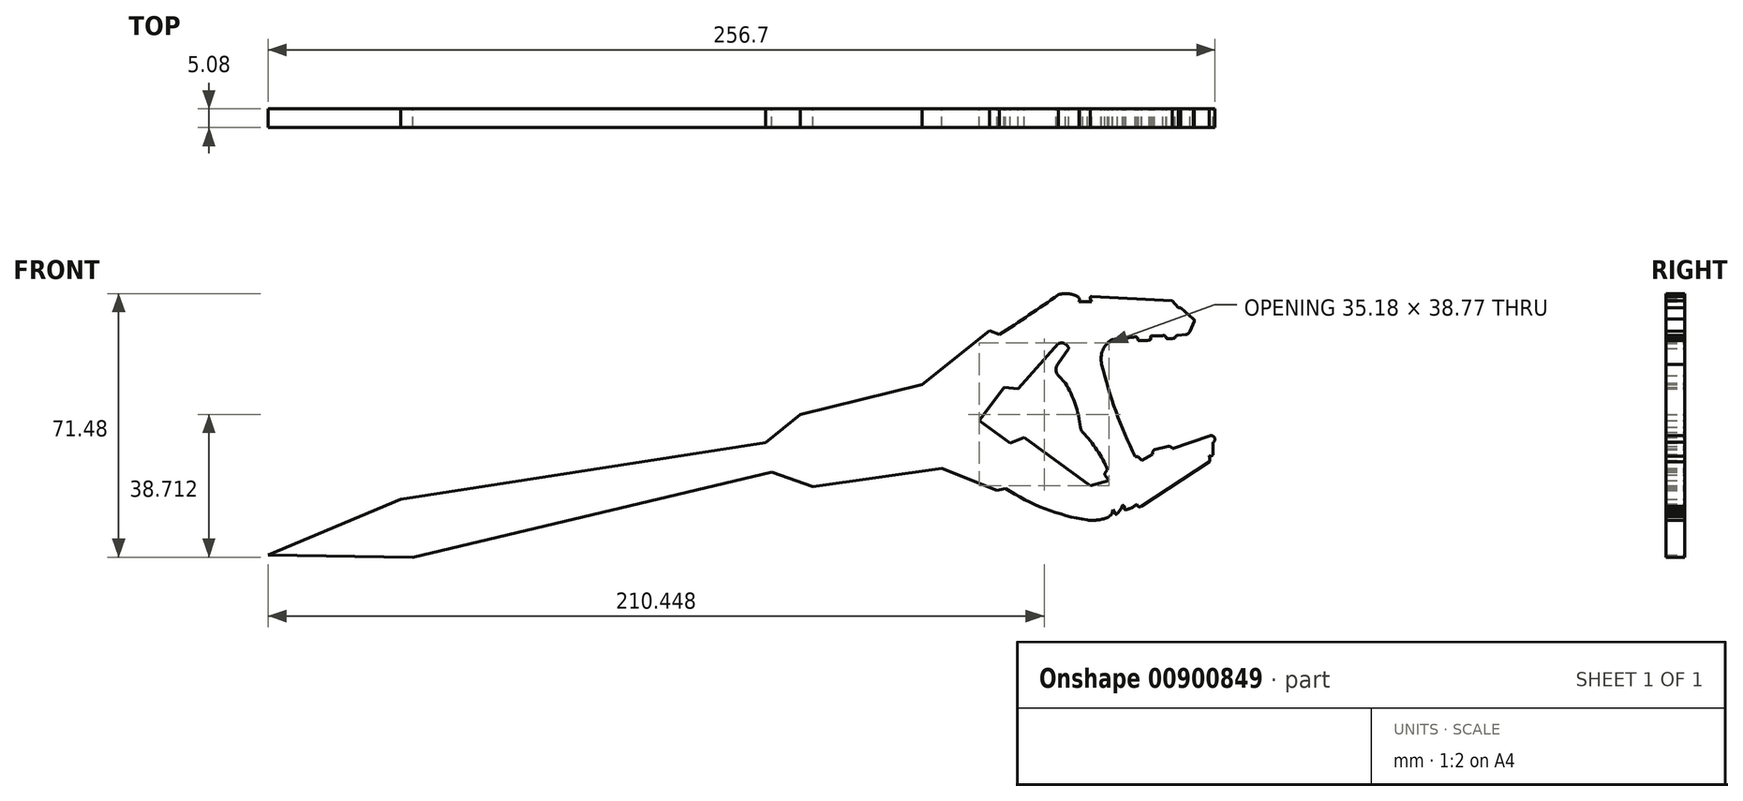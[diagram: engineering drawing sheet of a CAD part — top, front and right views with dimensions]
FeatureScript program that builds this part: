
annotation { "Feature Type Name" : "Feature", "Feature Type Description" : "" }
export const myFeature = defineFeature(function(context is Context, id is Id, definition is map)
    precondition{}
    {
        {
            var Q0;
            Q0=qCreatedBy(makeId("Front.planeOp"),FACE);
            var sketch = newSketch(context, id + "F0", { "sketchPlane" : qUnion([Q0])});
            skLineSegment(sketch, "E0", {"start": v(100.4, 44.75) * mm, "end": v(122.37, 43.65) * mm});
            skLineSegment(sketch, "E1", {"start": v(113.9, -12.05) * mm, "end": v(132.4, 0) * mm});
            skLineSegment(sketch, "E2", {"start": v(21.52, 12.73) * mm, "end": v(54.53, 20.95) * mm});
            skLineSegment(sketch, "E3", {"start": v(54.53, 20.95) * mm, "end": v(72.8, 35.55) * mm});
            skLineSegment(sketch, "E4", {"start": v(21.52, 12.73) * mm, "end": v(12.13, 5.19) * mm});
            skLineSegment(sketch, "E5", {"start": v(13.74, -2.79) * mm, "end": v(24.96, -6.78) * mm});
            skLineSegment(sketch, "E6", {"start": v(24.96, -6.78) * mm, "end": v(59.8, -1.87) * mm});
            skLineSegment(sketch, "E7", {"start": v(59.8, -1.87) * mm, "end": v(74.78, -7.84) * mm});
            skLineSegment(sketch, "E8", {"start": v(74.78, -7.84) * mm, "end": v(77.16, -7.24) * mm});
            skLineSegment(sketch, "E9", {"start": v(12.13, 5.19) * mm, "end": v(-86.83, -10.15) * mm});
            skLineSegment(sketch, "E10", {"start": v(-86.83, -10.15) * mm, "end": v(-122.84, -25.28) * mm});
            skLineSegment(sketch, "E11", {"start": v(72.8, 35.55) * mm, "end": v(75.47, 34.46) * mm});
            skLineSegment(sketch, "E12", {"start": v(76.66, 20.14) * mm, "end": v(70.02, 11.15) * mm});
            skLineSegment(sketch, "E13", {"start": v(70.02, 11.15) * mm, "end": v(78.32, 5.02) * mm});
            skLineSegment(sketch, "E14", {"start": v(78.32, 5.02) * mm, "end": v(82.2, 6.57) * mm});
            skLineSegment(sketch, "E15", {"start": v(82.2, 6.57) * mm, "end": v(100.16, -6.56) * mm});
            skLineSegment(sketch, "E16", {"start": v(100.16, -6.56) * mm, "end": v(105.2, -5.08) * mm});
            skLineSegment(sketch, "E17", {"start": v(76.66, 20.14) * mm, "end": v(81.19, 19.7) * mm});
            skLineSegment(sketch, "E18", {"start": v(91.5, 32.04) * mm, "end": v(80.58, 19.75) * mm});
            skLineSegment(sketch, "E19", {"start": v(105.2, -5.08) * mm, "end": v(104.05, -3.66) * mm});
            skArc(sketch, "E20", {"start": v(75.47, 34.46) * mm, "mid": v(83.52, 39.77) * mm, "end": v(91.45, 45.24) * mm});
            skArc(sketch, "E21", {"start": v(97.07, 44.48) * mm, "mid": v(94.35, 45.54) * mm, "end": v(91.45, 45.24) * mm});
            skArc(sketch, "E22", {"start": v(97.07, 43.35) * mm, "mid": v(97.13, 43.91) * mm, "end": v(97.07, 44.48) * mm});
            skLineSegment(sketch, "E23", {"start": v(97.07, 43.35) * mm, "end": v(100.5, 43.35) * mm});
            skLineSegment(sketch, "E24", {"start": v(100.5, 43.35) * mm, "end": v(100.14, 44.2) * mm});
            skArc(sketch, "E25", {"start": v(100.4, 44.75) * mm, "mid": v(100.1, 44.56) * mm, "end": v(100.14, 44.2) * mm});
            skArc(sketch, "E26", {"start": v(106.03, 33.12) * mm, "mid": v(103.5, 30.22) * mm, "end": v(103.2, 26.38) * mm});
            skArc(sketch, "E27", {"start": v(103.2, 26.38) * mm, "mid": v(107.04, 13.64) * mm, "end": v(112.26, 1.4) * mm});
            skArc(sketch, "E28", {"start": v(94.26, 30.67) * mm, "mid": v(93.2, 32) * mm, "end": v(91.5, 32.04) * mm});
            skArc(sketch, "E29", {"start": v(117.44, 3.2) * mm, "mid": v(117.03, 2.65) * mm, "end": v(117.05, 1.97) * mm});
            skLineSegment(sketch, "E30", {"start": v(117.44, 3.2) * mm, "end": v(121.18, 4.1) * mm});
            skArc(sketch, "E31", {"start": v(122.37, 3.54) * mm, "mid": v(121.87, 4.03) * mm, "end": v(121.18, 4.1) * mm});
            skLineSegment(sketch, "E32", {"start": v(122.37, 3.54) * mm, "end": v(132.3, 6.92) * mm});
            skArc(sketch, "E33", {"start": v(133.4, 5.23) * mm, "mid": v(133.7, 6.63) * mm, "end": v(132.3, 6.92) * mm});
            skLineSegment(sketch, "E34", {"start": v(133.4, 5.23) * mm, "end": v(133.4, 2.2) * mm});
            skArc(sketch, "E35", {"start": v(132.34, 1.6) * mm, "mid": v(133.05, 1.58) * mm, "end": v(133.4, 2.2) * mm});
            skArc(sketch, "E36", {"start": v(132.4, 0) * mm, "mid": v(132.48, 0.8) * mm, "end": v(132.34, 1.6) * mm});
            skArc(sketch, "E37", {"start": v(77.16, -7.24) * mm, "mid": v(87.78, -12.75) * mm, "end": v(99.34, -15.84) * mm});
            skArc(sketch, "E38", {"start": v(99.34, -15.84) * mm, "mid": v(102.3, -15.8) * mm, "end": v(105.12, -14.96) * mm});
            skPoint(sketch, "E39.start.orphan", {"position": v(107.25, -13.94) * mm});
            skPoint(sketch, "E40.orphan", {"position": v(107.24, -13.94) * mm});
            skPoint(sketch, "E41.end.orphan", {"position": v(105.95, -12.54) * mm});
            skPoint(sketch, "E42.end.orphan", {"position": v(105.95, -14.27) * mm});
            skArc(sketch, "E43", {"start": v(105.12, -14.96) * mm, "mid": v(105.9, -14.1) * mm, "end": v(106.18, -12.98) * mm});
            skLineSegment(sketch, "E44", {"start": v(106.18, -12.98) * mm, "end": v(106.77, -14.03) * mm});
            skArc(sketch, "E45", {"start": v(106.77, -14.03) * mm, "mid": v(107.1, -14.23) * mm, "end": v(107.44, -14.03) * mm});
            skArc(sketch, "E46", {"start": v(107.44, -14.03) * mm, "mid": v(108.28, -13.02) * mm, "end": v(108.82, -11.83) * mm});
            skArc(sketch, "E47", {"start": v(109.31, -12.56) * mm, "mid": v(109.27, -12.06) * mm, "end": v(108.82, -11.83) * mm});
            skArc(sketch, "E48", {"start": v(109.31, -12.56) * mm, "mid": v(109.4, -12.95) * mm, "end": v(109.78, -13.05) * mm});
            skArc(sketch, "E49", {"start": v(109.78, -13.05) * mm, "mid": v(111.4, -12.43) * mm, "end": v(112.85, -11.5) * mm});
            skArc(sketch, "E50", {"start": v(112.85, -11.5) * mm, "mid": v(113.16, -12.19) * mm, "end": v(113.9, -12.05) * mm});
            skLineSegment(sketch, "E51", {"start": v(117.05, 1.97) * mm, "end": v(114.12, 0.32) * mm});
            skLineSegment(sketch, "E52", {"start": v(114.12, 0.32) * mm, "end": v(113.04, 1.4) * mm});
            skLineSegment(sketch, "E53", {"start": v(113.04, 1.4) * mm, "end": v(112.26, 1.4) * mm});
            skArc(sketch, "E54", {"start": v(106.03, 33.12) * mm, "mid": v(109.29, 33.45) * mm, "end": v(112.53, 33.93) * mm});
            skArc(sketch, "E55", {"start": v(113, 33.07) * mm, "mid": v(112.86, 33.55) * mm, "end": v(112.53, 33.93) * mm});
            skArc(sketch, "E56", {"start": v(113, 33.07) * mm, "mid": v(113.02, 32.95) * mm, "end": v(113.11, 32.86) * mm});
            skArc(sketch, "E57", {"start": v(113.11, 32.86) * mm, "mid": v(114.6, 32.8) * mm, "end": v(116.1, 32.96) * mm});
            skArc(sketch, "E58", {"start": v(116.1, 32.96) * mm, "mid": v(116.3, 33.01) * mm, "end": v(116.44, 33.19) * mm});
            skArc(sketch, "E59", {"start": v(116.55, 34.17) * mm, "mid": v(116.48, 33.68) * mm, "end": v(116.44, 33.19) * mm});
            skLineSegment(sketch, "E60", {"start": v(116.55, 34.17) * mm, "end": v(119.77, 34.17) * mm});
            skArc(sketch, "E61", {"start": v(120.68, 33.64) * mm, "mid": v(120.34, 34.1) * mm, "end": v(119.77, 34.17) * mm});
            skArc(sketch, "E62", {"start": v(120.68, 33.64) * mm, "mid": v(120.7, 33.5) * mm, "end": v(120.8, 33.4) * mm});
            skArc(sketch, "E63", {"start": v(120.8, 33.4) * mm, "mid": v(121.87, 33.35) * mm, "end": v(122.93, 33.5) * mm});
            skArc(sketch, "E64", {"start": v(122.93, 33.5) * mm, "mid": v(123.08, 33.6) * mm, "end": v(123.12, 33.77) * mm});
            skArc(sketch, "E65", {"start": v(123.9, 34.27) * mm, "mid": v(123.43, 34.14) * mm, "end": v(123.12, 33.77) * mm});
            skLineSegment(sketch, "E66", {"start": v(123.9, 34.27) * mm, "end": v(126, 34.46) * mm});
            skArc(sketch, "E67", {"start": v(126, 34.46) * mm, "mid": v(126.7, 34.75) * mm, "end": v(127.1, 35.4) * mm});
            skLineSegment(sketch, "E68", {"start": v(127.1, 35.4) * mm, "end": v(128.26, 38.1) * mm});
            skArc(sketch, "E69", {"start": v(128.26, 38.1) * mm, "mid": v(128.27, 38.46) * mm, "end": v(128.05, 38.74) * mm});
            skLineSegment(sketch, "E70", {"start": v(128.05, 38.74) * mm, "end": v(124.58, 41.76) * mm});
            skLineSegment(sketch, "E71", {"start": v(124.58, 41.76) * mm, "end": v(123.95, 41.76) * mm});
            skLineSegment(sketch, "E72", {"start": v(123.95, 41.76) * mm, "end": v(122.37, 43.65) * mm});
            skLineSegment(sketch, "E73", {"start": v(94.26, 30.67) * mm, "end": v(91.3, 26.51) * mm});
            skLineSegment(sketch, "E74", {"start": v(91.43, 23.29) * mm, "end": v(93.33, 21.3) * mm});
            skArc(sketch, "E75", {"start": v(91.3, 26.51) * mm, "mid": v(90.81, 24.88) * mm, "end": v(91.43, 23.29) * mm});
            skArc(sketch, "E76", {"start": v(97.42, 9.33) * mm, "mid": v(96.01, 15.53) * mm, "end": v(93.33, 21.3) * mm});
            skArc(sketch, "E77", {"start": v(97.42, 9.33) * mm, "mid": v(97.62, 8.62) * mm, "end": v(98, 8) * mm});
            skArc(sketch, "E78", {"start": v(104.85, -2.29) * mm, "mid": v(101.9, 3.17) * mm, "end": v(98, 8) * mm});
            skArc(sketch, "E79", {"start": v(104.85, -2.29) * mm, "mid": v(104.23, -2.84) * mm, "end": v(104.05, -3.66) * mm});
            skPoint(sketch, "E80", {"position": v(-56.52, -10.12) * mm});
            skPoint(sketch, "E81", {"position": v(43.95, 8.52) * mm});
            skPoint(sketch, "E82", {"position": v(-95.39, -20.14) * mm});
            skPoint(sketch, "E83", {"position": v(-65.23, -7.42) * mm});
            skLineSegment(sketch, "E84", {"start": v(-122.84, -25.28) * mm, "end": v(-83.53, -25.9) * mm});
            skLineSegment(sketch, "E85", {"start": v(-83.53, -25.9) * mm, "end": v(13.74, -2.79) * mm});
            skPoint(sketch, "E86", {"position": v(-62.34, -20.86) * mm});
            skSolve(sketch);
        }
        {
            var Q0;
            Q0=makeQuery(id+"F0.imprint","IMPRINT",FACE,{"disambiguationData":[TD([[makeQuery(id+"F0.imprint","IMPRINT",EDGE,{"derivedFrom":sQuery(id+"F0.wireOp",EDGE,"E0")}),-1.0]])]});
            extrude(context, id + "F1", {"entities" : qUnion([Q0]), "depth" : 5.08 * mm, "offsetDistance" : 25.4 * mm});
        }
    });
